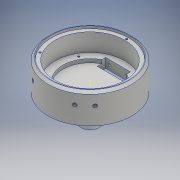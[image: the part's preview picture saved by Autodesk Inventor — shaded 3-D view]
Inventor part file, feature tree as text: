
AUTODESK INVENTOR PART (.ipt)
format: ipt  version: 2017 (Build 210142000, 142)  size: 281,600 bytes
history: native  units: mm
features: sketch x14, thread x10, extrude x7, plane x7, hole x7, projected_geometry x2, chamfer x1
ambient origin geometry x8: Origin, YZ Plane, XZ Plane, XY Plane, X Axis, Y Axis, Z Axis, Center Point
bodies: Solid1 (feature_tree)
feature tree (48):
  extrude  "Extrusion1"  Depth=25.0mm TaperAngle=0.0deg
  extrude  "Extrusion2"  Depth=17.0mm TaperAngle=0.0deg
  extrude  "Extrusion4"  Depth=35.0mm
  plane  "Work Plane1"
  extrude  "Extrusion7"  Depth=2.0mm TaperAngle=0.0deg
  chamfer  "Chamfer1"  Distance=2.0mm Angle=45.0deg
  hole  "Hole3"  [1 undecoded]
  hole  "Hole4"  [1 undecoded]
  thread  "Thread1"  [1 undecoded]
  thread  "Thread2"  [1 undecoded]
  thread  "Thread3"  [1 undecoded]
  thread  "Thread4"  [1 undecoded]
  thread  "Thread5"  [1 undecoded]
  thread  "Thread6"  [1 undecoded]
  sketch  "Sketch12"  dims[d54=1.6mm d55=6.0mm d56=4.0mm d57=2.0mm d58=90.0deg d59=5.0mm d60=20.594885mm d61=61.315mm d62=30.0mm d64=360.0deg]
  plane  "Work Plane2"
  plane  "Work Plane3"
  plane  "Work Plane4"
  plane  "Work Plane5"
  hole  "Hole5"  [1 undecoded]
  hole  "Hole6"  [1 undecoded]
  hole  "Hole9"  [1 undecoded]
  hole  "Hole10"  [1 undecoded]
  thread  "Thread7"  [1 undecoded]
  thread  "Thread8"  [1 undecoded]
  extrude  "Extrusion8"  Depth=14.5mm
  thread  "Thread11"  [1 undecoded]
  thread  "Thread12"  [1 undecoded]
  plane  "Work Plane6"
  sketch  "Sketch21"  dims[d88=3.0mm d89=6.0mm d90=4.0mm d91=2.0mm d92=90.0deg d93=4.0mm d94=20.594885mm d95=14.5mm]
  sketch  "Sketch22"  dims[d96=3.0mm d97=6.0mm d98=4.0mm d99=2.0mm d100=90.0deg d101=4.0mm d102=20.594885mm d117=10.0mm d118=0.0mm d119=10.0mm d120=0.0mm d125=15.0mm]
  extrude  "Extrusion10"  Depth=10.0mm TaperAngle=0.0deg
  hole  "Hole12"  [1 undecoded]
  plane  "Work Plane7"
  extrude  "Extrusion11"  Depth=5.0mm
  sketch  "Sketch1"  dims[d0=70.0mm d1=25.0mm d2=0.0mm]
  sketch  "Sketch2"  dims[d3=47.0mm d8=17.0mm d9=0.0mm]
  sketch  "Sketch8"  dims[d13=3.0mm d14=0.0mm d32=35.0mm]
  sketch  "Sketch10"  dims[d36=65.0mm d37=2.0mm d38=0.0mm d46=2.0mm d47=2.0mm d48=45.0deg]
  projected_geometry  "Projected Loop4"
  sketch  "Sketch11"  dims[d49=51.762mm d50=30.0mm d52=360.0deg]
  sketch  "Sketch13"  dims[d66=1.6mm d67=6.0mm d68=4.0mm d69=2.0mm d70=90.0deg d71=5.0mm d72=20.594885mm d73=10.0mm d74=0.0mm d75=10.0mm d76=0.0mm d77=10.0mm d78=0.0mm d79=10.0mm d80=0.0mm d81=10.0mm d82=0.0mm]
  sketch  "Sketch14"  dims[d83=10.0mm d84=0.0mm d85=6.981317mm]
  sketch  "Sketch17"  dims[d86=60.0deg d87=14.5mm]
  sketch  "Sketch23"  dims[d126=22.2mm d127=0.0mm d128=14.5mm d129=14.5mm]
  sketch  "Sketch24"  dims[d130=3.0mm d131=6.0mm d132=4.0mm d133=2.0mm d134=90.0deg d135=4.0mm d136=20.594885mm]
  sketch  "Sketch25"  dims[d137=3.0mm d138=6.0mm d139=4.0mm d140=2.0mm d141=90.0deg d142=4.0mm d143=20.594885mm d144=10.0mm d145=0.0mm d146=10.0mm d147=0.0mm d148=45.762433mm d164=35.0mm d173=58.5mm d175=47.2mm d176=21.0mm d177=7.0mm d178=10.0mm d179=0.0mm d180=15.0mm d181=2.1mm d182=2.1mm d183=4.1mm d184=4.1mm d185=7.5mm d186=7.5mm d187=2.1mm d188=6.0mm d189=4.0mm d190=2.0mm d191=90.0deg d192=8.0mm d193=20.594885mm d194=35.0mm d195=5.0mm d196=2.0mm d197=0.0mm d172=1.0mm]
  projected_geometry  "Projected Loop6"
note: 17 required parameter values undecoded (feature->parameter linkage not recoverable at this tier; creation-order binding heuristic only, values carry confidence <= 0.55)
